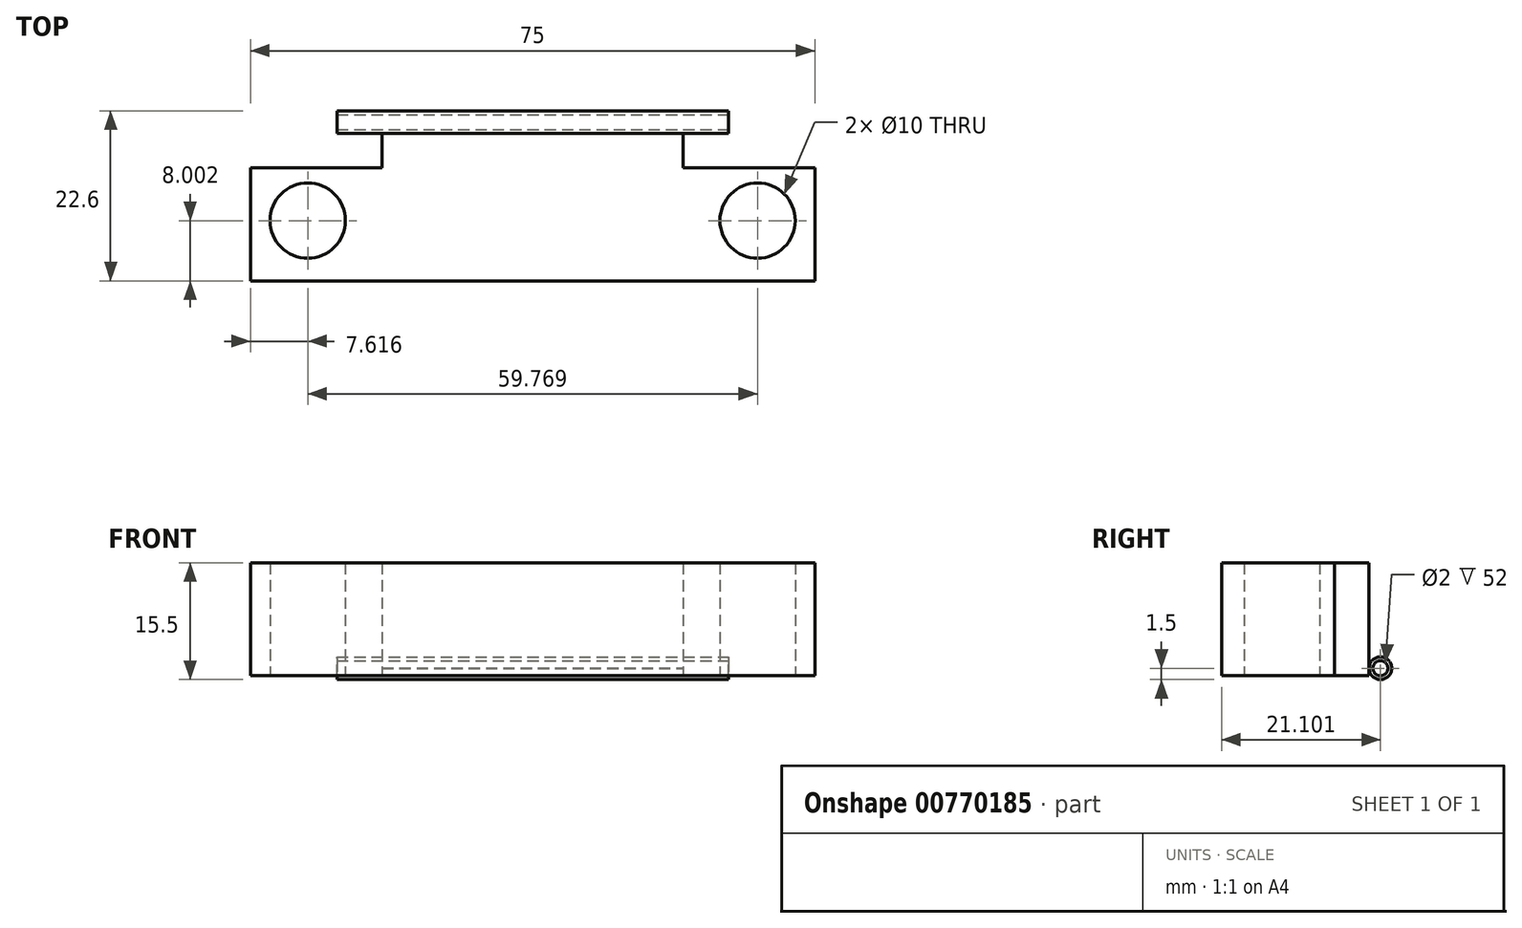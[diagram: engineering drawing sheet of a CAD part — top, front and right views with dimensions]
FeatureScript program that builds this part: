
annotation { "Feature Type Name" : "Feature", "Feature Type Description" : "" }
export const myFeature = defineFeature(function(context is Context, id is Id, definition is map)
    precondition{}
    {
        {
            var Q0;
            Q0=qCreatedBy(makeId("Top.planeOp"),FACE);
            var sketch = newSketch(context, id + "F0", { "sketchPlane" : qUnion([Q0])});
            skPoint(sketch, "E0", {"position": v(0, 0) * mm});
            skCircle(sketch, "E1", {"center": v(0, 171) * mm, "radius": 171 * mm, "construction": true});
            skCircle(sketch, "E2", {"center": v(0, 0) * mm, "radius": 30 * mm, "construction": true});
            skLineSegment(sketch, "E3", {"start": v(-37.5, -5.37) * mm, "end": v(-37.5, 9.63) * mm});
            skLineSegment(sketch, "E4", {"start": v(-37.5, 9.63) * mm, "end": v(-20, 9.63) * mm});
            skLineSegment(sketch, "E5", {"start": v(-20, 9.63) * mm, "end": v(-20, 14.23) * mm});
            skLineSegment(sketch, "E6", {"start": v(-20, 14.23) * mm, "end": v(20, 14.23) * mm});
            skLineSegment(sketch, "E7", {"start": v(20, 14.23) * mm, "end": v(20, 9.63) * mm});
            skLineSegment(sketch, "E8", {"start": v(20, 9.63) * mm, "end": v(37.5, 9.63) * mm});
            skLineSegment(sketch, "E9", {"start": v(37.5, 9.63) * mm, "end": v(37.5, -5.37) * mm});
            skLineSegment(sketch, "E10", {"start": v(37.5, -5.37) * mm, "end": v(-37.5, -5.37) * mm});
            skPoint(sketch, "E11.positionSnap0", {"position": v(0, 14.23) * mm});
            skPoint(sketch, "E12", {"position": v(0, -5.37) * mm});
            skPoint(sketch, "E13", {"position": v(-29.88, 2.63) * mm});
            skPoint(sketch, "E14", {"position": v(29.88, 2.63) * mm});
            skCircle(sketch, "E15", {"center": v(29.88, 2.63) * mm, "radius": 5 * mm});
            skCircle(sketch, "E16", {"center": v(-29.88, 2.63) * mm, "radius": 5 * mm});
            skSolve(sketch);
        }
        {
            var Q0;
            Q0=makeQuery(id+"F0.imprint","IMPRINT",FACE,{"disambiguationData":[TD([[makeQuery(id+"F0.imprint","IMPRINT",EDGE,{"derivedFrom":sQuery(id+"F0.wireOp",EDGE,"e0JXxabs-A6ob-Ss8H-2lH8-nyCzjPuL4Hk7")}),-1.0]])]});
            var Q1;
            Q1=makeQuery(id+"F0.imprint","IMPRINT",FACE,{"disambiguationData":[TD([[makeQuery(id+"F0.imprint","IMPRINT",EDGE,{"derivedFrom":sQuery(id+"F0.wireOp",EDGE,"E3")}),-1.0]])]});
            extrude(context, id + "F1", {"entities" : qUnion([Q0, Q1]), "depth" : 15 * mm, "offsetDistance" : 25 * mm});
        }
        {
            var Q0;
            Q0=makeQuery(id+"F1.opExtrude","SWEPT_FACE",FACE,{"disambiguationData":[OSD([sQuery(id+"F0.wireOp",EDGE,"E3")])]});
            cPlane(context, id + "F2", {"entities" : qUnion([Q0]), "cplaneType" : CPlaneType.OFFSET, "offset" : 75 / 2 * mm, "oppositeDirection" : true, "width" : 150 * mm, "height" : 150 * mm});
        }
        {
            var Q0;
            Q0=qCreatedBy(id+"F2.planeOp",FACE);
            var sketch = newSketch(context, id + "F3", { "sketchPlane" : qUnion([Q0])});
            skCircle(sketch, "E17", {"center": v(-15.73, 1) * mm, "radius": 1 * mm});
            skCircle(sketch, "E18", {"center": v(-15.73, 1) * mm, "radius": 1.5 * mm});
            skSolve(sketch);
        }
        {
            var Q0;
            Q0=makeQuery(id+"F3.imprint","IMPRINT",FACE,{"disambiguationData":[TD([[makeQuery(id+"F3.imprint","IMPRINT",EDGE,{"derivedFrom":sQuery(id+"F3.wireOp",EDGE,"E17")}),-1.0]])]});
            extrude(context, id + "F4", {"entities" : qUnion([Q0]), "operationType" : NewBodyOperationType.ADD, "endBound" : BoundingType.SYMMETRIC, "depth" : 52 * mm, "offsetDistance" : 25 * mm});
        }
    });
